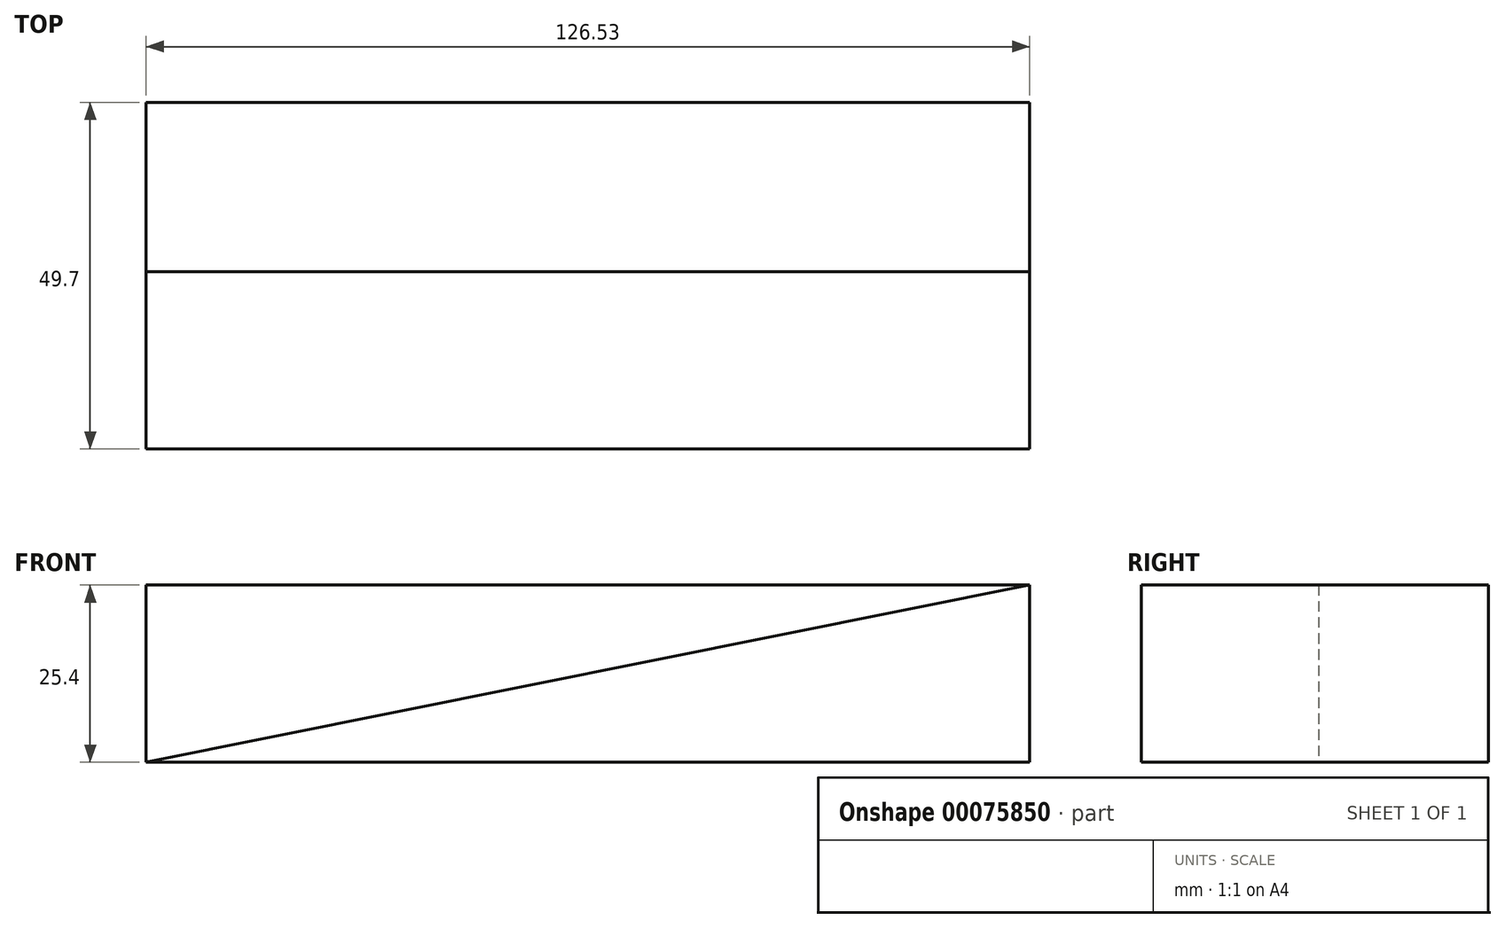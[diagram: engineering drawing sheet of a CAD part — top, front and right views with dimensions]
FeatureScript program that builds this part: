
annotation { "Feature Type Name" : "Feature", "Feature Type Description" : "" }
export const myFeature = defineFeature(function(context is Context, id is Id, definition is map)
    precondition{}
    {
        {
            var Q0;
            Q0=qCreatedBy(makeId("Top.planeOp"),FACE);
            var sketch = newSketch(context, id + "F0", { "sketchPlane" : qUnion([Q0])});
            skLineSegment(sketch, "E0.bottom", {"start": v(-67.96, 13.35) * mm, "end": v(58.57, 13.35) * mm});
            skLineSegment(sketch, "E0.top", {"start": v(-67.96, -36.35) * mm, "end": v(58.57, -36.35) * mm});
            skLineSegment(sketch, "E0.left", {"start": v(-67.96, 13.35) * mm, "end": v(-67.96, -36.35) * mm});
            skLineSegment(sketch, "E0.right", {"start": v(58.57, 13.35) * mm, "end": v(58.57, -36.35) * mm});
            skSolve(sketch);
        }
        {
            var Q0;
            Q0 = qSketchRegion(id + "F0", true);
            extrude(context, id + "F1", {"entities" : qUnion([Q0]), "depth" : 25.4 * mm});
        }
        {
            var Q0;
            Q0=makeQuery(id+"F1.opExtrude","SWEPT_FACE",FACE,{"disambiguationData":[OSD([sQuery(id+"F0.wireOp",EDGE,"E0.top")])]});
            var sketch = newSketch(context, id + "F2", { "sketchPlane" : qUnion([Q0])});
            skLineSegment(sketch, "E1", {"start": v(58.57, 25.4) * mm, "end": v(-67.96, 0) * mm});
            skSolve(sketch);
        }
        {
            var Q0;
            Q0=makeQuery(id+"F2.imprint","IMPRINT",FACE,{"disambiguationData":[TD([[makeQuery(id+"F2.imprint","IMPRINT",EDGE,{"derivedFrom":sQuery(id+"F2.wireOp",EDGE,"E1")}),-1.0]])]});
            extrude(context, id + "F3", {"entities" : qUnion([Q0]), "operationType" : NewBodyOperationType.REMOVE, "oppositeDirection" : true, "depth" : 25.4 * mm});
        }
    });
